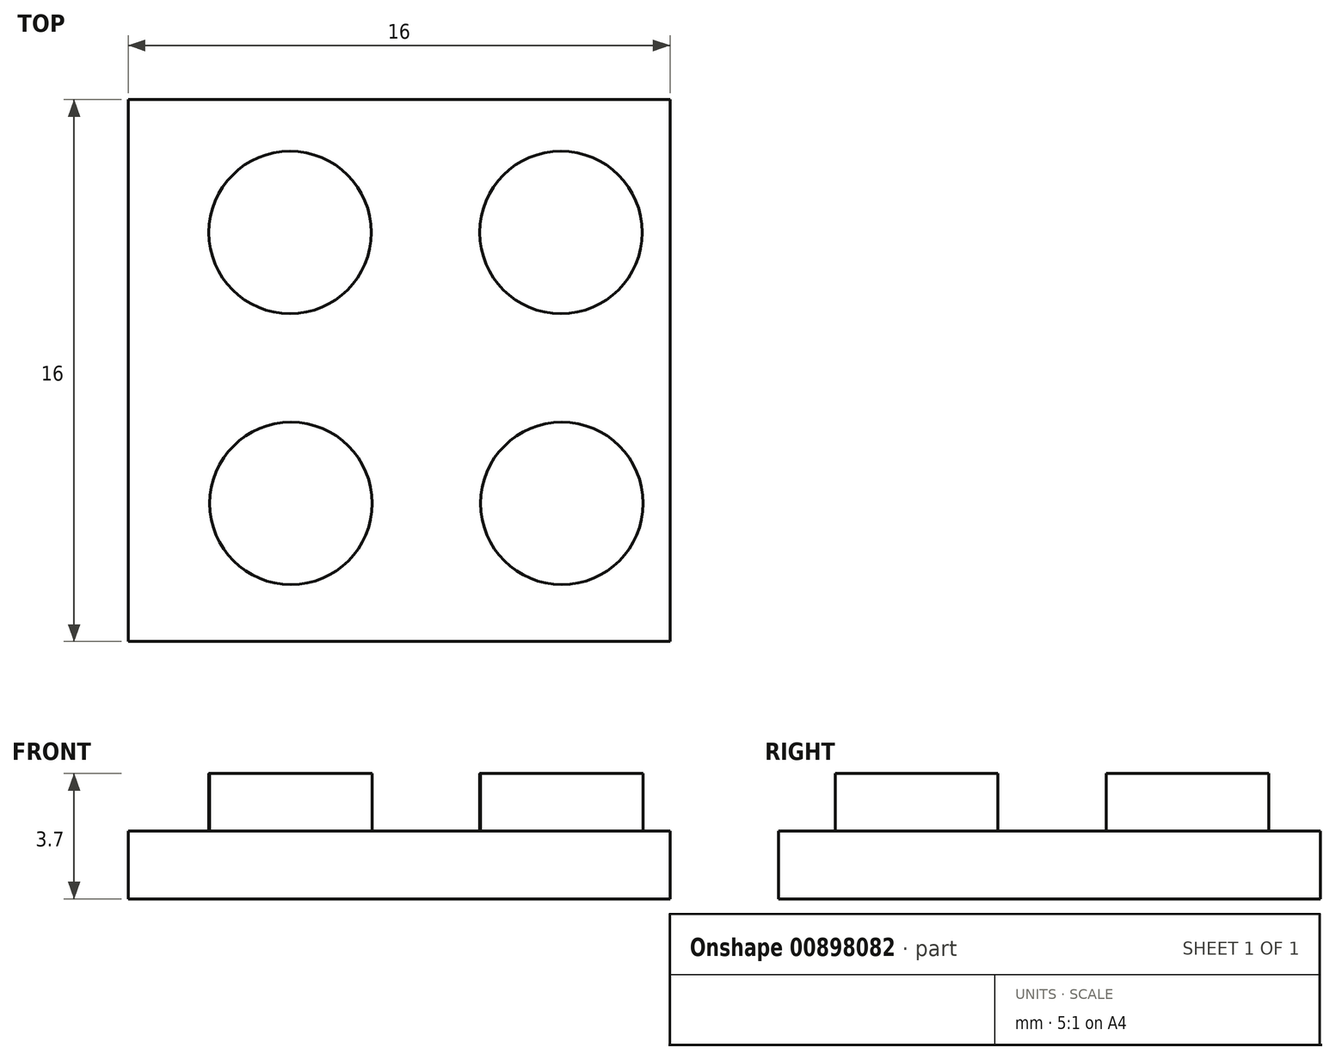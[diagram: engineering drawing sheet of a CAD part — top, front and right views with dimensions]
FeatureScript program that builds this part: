
annotation { "Feature Type Name" : "Feature", "Feature Type Description" : "" }
export const myFeature = defineFeature(function(context is Context, id is Id, definition is map)
    precondition{}
    {
        {
            var Q0;
            Q0=qCreatedBy(makeId("Top.planeOp"),FACE);
            var sketch = newSketch(context, id + "F0", { "sketchPlane" : qUnion([Q0])});
            skLineSegment(sketch, "E0.bottom", {"start": v(0, 0) * mm, "end": v(16, 0) * mm});
            skLineSegment(sketch, "E0.top", {"start": v(0, -16) * mm, "end": v(16, -16) * mm});
            skLineSegment(sketch, "E0.left", {"start": v(0, 0) * mm, "end": v(0, -16) * mm});
            skLineSegment(sketch, "E0.right", {"start": v(16, 0) * mm, "end": v(16, -16) * mm});
            skCircle(sketch, "E1", {"center": v(4.78, -3.92) * mm, "radius": 2.4 * mm});
            skCircle(sketch, "E2.1.0.0", {"center": v(12.78, -3.92) * mm, "radius": 2.4 * mm});
            skLineSegment(sketch, "E2.direction1", {"start": v(4.78, -3.92) * mm, "end": v(12.78, -3.92) * mm, "construction": true});
            skCircle(sketch, "E3.1.0.0", {"center": v(12.8, -11.92) * mm, "radius": 2.4 * mm});
            skCircle(sketch, "E3.1.0.1", {"center": v(4.8, -11.92) * mm, "radius": 2.4 * mm});
            skLineSegment(sketch, "E3.direction1", {"start": v(4.78, -3.92) * mm, "end": v(4.8, -11.92) * mm, "construction": true});
            skSolve(sketch);
        }
        {
            var Q0;
            Q0=makeQuery(id+"F0.imprint","IMPRINT",FACE,{"disambiguationData":[TD([[makeQuery(id+"F0.imprint","IMPRINT",EDGE,{"derivedFrom":sQuery(id+"F0.wireOp",EDGE,"E3.1.0.0")}),1.0]])]});
            var Q1;
            Q1=makeQuery(id+"F0.imprint","IMPRINT",FACE,{"disambiguationData":[TD([[makeQuery(id+"F0.imprint","IMPRINT",EDGE,{"derivedFrom":sQuery(id+"F0.wireOp",EDGE,"E2.1.0.0")}),1.0]])]});
            var Q2;
            Q2=makeQuery(id+"F0.imprint","IMPRINT",FACE,{"disambiguationData":[TD([[makeQuery(id+"F0.imprint","IMPRINT",EDGE,{"derivedFrom":sQuery(id+"F0.wireOp",EDGE,"E1")}),1.0]])]});
            var Q3;
            Q3=makeQuery(id+"F0.imprint","IMPRINT",FACE,{"disambiguationData":[TD([[makeQuery(id+"F0.imprint","IMPRINT",EDGE,{"derivedFrom":sQuery(id+"F0.wireOp",EDGE,"E3.1.0.1")}),1.0]])]});
            extrude(context, id + "F1", {"entities" : qUnion([Q0, Q1, Q2, Q3]), "depth" : 1.7 * mm, "offsetDistance" : 25 * mm});
        }
        {
            var Q0;
            Q0=makeQuery(id+"F0.imprint","IMPRINT",FACE,{"disambiguationData":[TD([[makeQuery(id+"F0.imprint","IMPRINT",EDGE,{"derivedFrom":sQuery(id+"F0.wireOp",EDGE,"E0.bottom")}),-1.0]])]});
            var Q1;
            Q1=makeQuery(id+"F0.imprint","IMPRINT",FACE,{"disambiguationData":[TD([[makeQuery(id+"F0.imprint","IMPRINT",EDGE,{"derivedFrom":sQuery(id+"F0.wireOp",EDGE,"E2.1.0.0")}),1.0]])]});
            var Q2;
            Q2=makeQuery(id+"F0.imprint","IMPRINT",FACE,{"disambiguationData":[TD([[makeQuery(id+"F0.imprint","IMPRINT",EDGE,{"derivedFrom":sQuery(id+"F0.wireOp",EDGE,"E3.1.0.0")}),1.0]])]});
            var Q3;
            Q3=makeQuery(id+"F0.imprint","IMPRINT",FACE,{"disambiguationData":[TD([[makeQuery(id+"F0.imprint","IMPRINT",EDGE,{"derivedFrom":sQuery(id+"F0.wireOp",EDGE,"E3.1.0.1")}),1.0]])]});
            var Q4;
            Q4=makeQuery(id+"F0.imprint","IMPRINT",FACE,{"disambiguationData":[TD([[makeQuery(id+"F0.imprint","IMPRINT",EDGE,{"derivedFrom":sQuery(id+"F0.wireOp",EDGE,"E1")}),1.0]])]});
            extrude(context, id + "F2", {"entities" : qUnion([Q0, Q1, Q2, Q3, Q4]), "oppositeDirection" : true, "depth" : 2 * mm, "offsetDistance" : 25 * mm});
        }
    });
